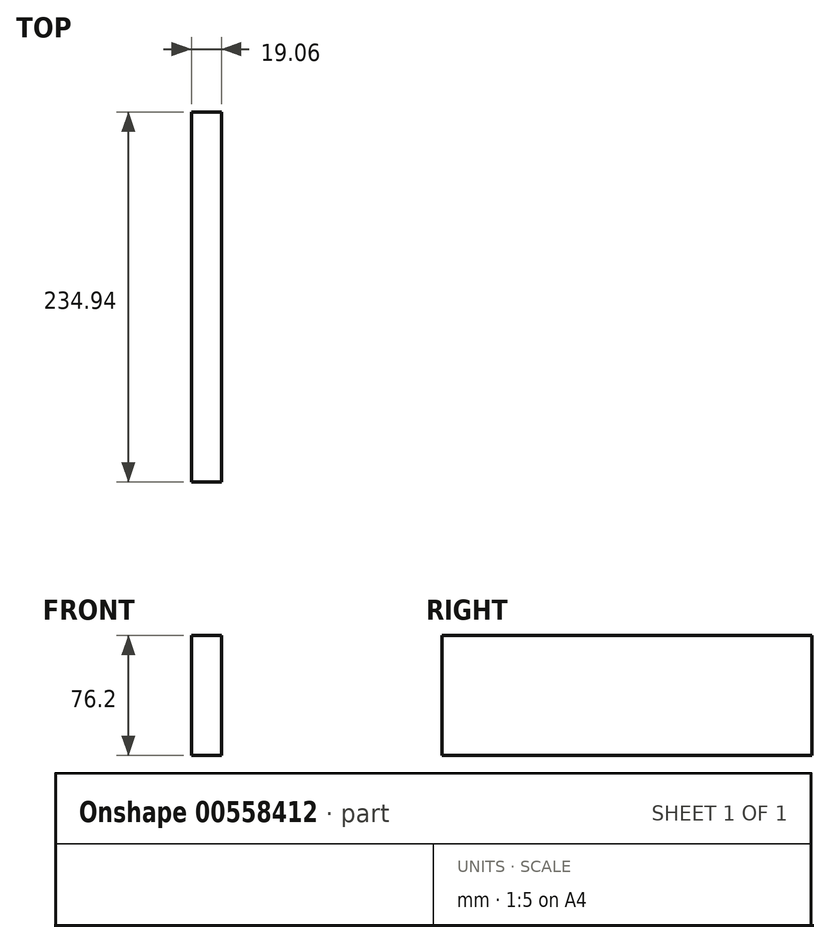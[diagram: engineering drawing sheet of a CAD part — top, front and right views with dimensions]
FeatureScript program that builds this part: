
annotation { "Feature Type Name" : "Feature", "Feature Type Description" : "" }
export const myFeature = defineFeature(function(context is Context, id is Id, definition is map)
    precondition{}
    {
        {
            var Q0;
            Q0=qCreatedBy(makeId("Right.planeOp"),FACE);
            var sketch = newSketch(context, id + "F0", { "sketchPlane" : qUnion([Q0])});
            skLineSegment(sketch, "E0.bottom", {"start": v(117.48, 38.1) * mm, "end": v(-117.48, 38.1) * mm});
            skLineSegment(sketch, "E0.top", {"start": v(117.48, -38.1) * mm, "end": v(-117.48, -38.1) * mm});
            skLineSegment(sketch, "E0.left", {"start": v(117.48, 38.1) * mm, "end": v(117.48, -38.1) * mm});
            skLineSegment(sketch, "E0.right", {"start": v(-117.48, 38.1) * mm, "end": v(-117.48, -38.1) * mm});
            skPoint(sketch, "E0.middle", {"position": v(0, 0) * mm});
            skSolve(sketch);
        }
        {
            var Q0;
            Q0=makeQuery(id+"F0.imprint","IMPRINT",FACE,{"disambiguationData":[TD([[makeQuery(id+"F0.imprint","IMPRINT",EDGE,{"derivedFrom":sQuery(id+"F0.wireOp",EDGE,"E0.bottom")}),1.0]])]});
            extrude(context, id + "F1", {"entities" : qUnion([Q0]), "endBound" : BoundingType.SYMMETRIC, "depth" : 19.05 * mm, "offsetDistance" : 25.4 * mm});
        }
    });
